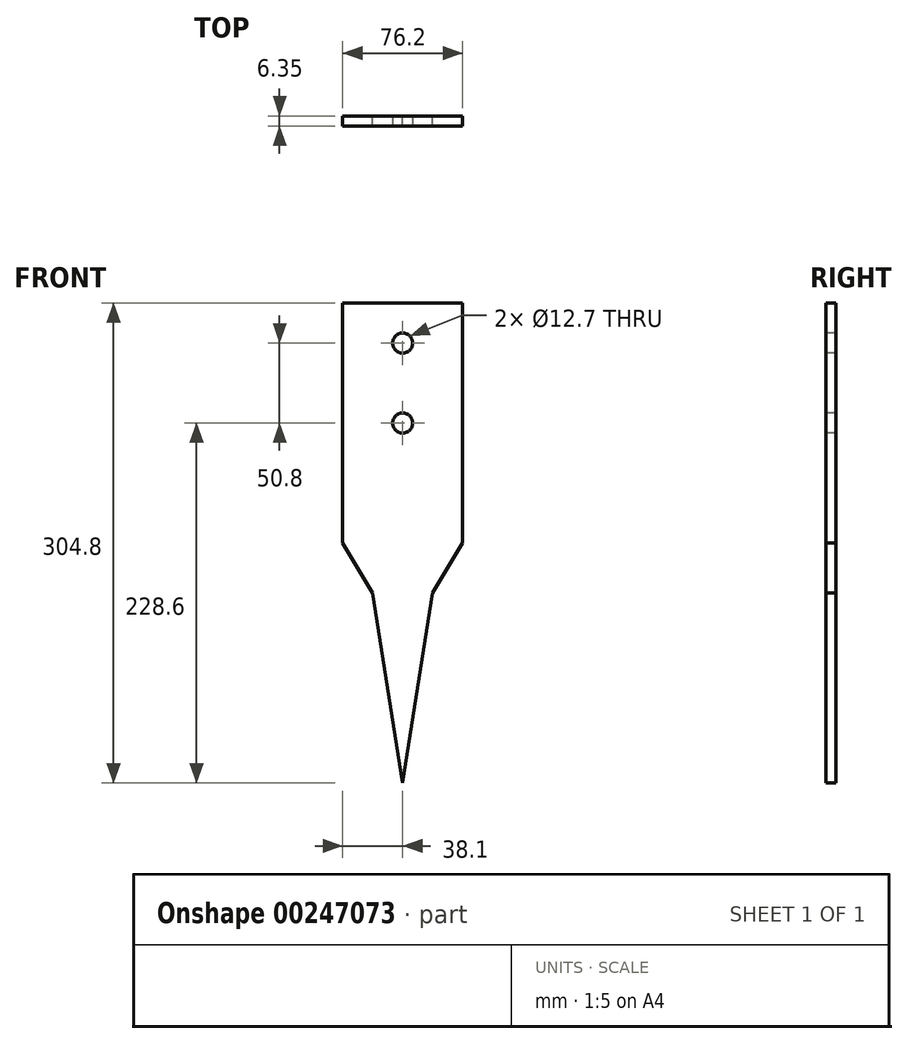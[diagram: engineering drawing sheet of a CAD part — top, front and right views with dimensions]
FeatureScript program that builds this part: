
annotation { "Feature Type Name" : "Feature", "Feature Type Description" : "" }
export const myFeature = defineFeature(function(context is Context, id is Id, definition is map)
    precondition{}
    {
        {
            var Q0;
            Q0=qCreatedBy(makeId("Front.planeOp"),FACE);
            var sketch = newSketch(context, id + "F0", { "sketchPlane" : qUnion([Q0])});
            skLineSegment(sketch, "E0.bottom", {"start": v(38.1, 76.2) * mm, "end": v(-38.1, 76.2) * mm});
            skLineSegment(sketch, "E0.top", {"start": v(38.1, -76.2) * mm, "end": v(-38.1, -76.2) * mm});
            skLineSegment(sketch, "E0.left", {"start": v(38.1, 76.2) * mm, "end": v(38.1, -76.2) * mm});
            skLineSegment(sketch, "E0.right", {"start": v(-38.1, 76.2) * mm, "end": v(-38.1, -76.2) * mm});
            skPoint(sketch, "E0.middle", {"position": v(0, 0) * mm});
            skLineSegment(sketch, "E1", {"start": v(38.1, -76.2) * mm, "end": v(19.05, -107.95) * mm});
            skLineSegment(sketch, "E2", {"start": v(19.05, -107.95) * mm, "end": v(0, -228.6) * mm});
            skLineSegment(sketch, "E3", {"start": v(0, -228.6) * mm, "end": v(-19.05, -107.95) * mm});
            skLineSegment(sketch, "E4", {"start": v(-19.05, -107.95) * mm, "end": v(-38.1, -76.2) * mm});
            skSolve(sketch);
        }
        {
            var Q0;
            Q0=makeQuery(id+"F0.imprint","IMPRINT",FACE,{"disambiguationData":[TD([[makeQuery(id+"F0.imprint","IMPRINT",EDGE,{"derivedFrom":sQuery(id+"F0.wireOp",EDGE,"E0.bottom")}),1.0]])]});
            var Q1;
            Q1=makeQuery(id+"F0.imprint","IMPRINT",FACE,{"disambiguationData":[TD([[makeQuery(id+"F0.imprint","IMPRINT",EDGE,{"derivedFrom":sQuery(id+"F0.wireOp",EDGE,"E0.top")}),1.0]])]});
            extrude(context, id + "F1", {"entities" : qUnion([Q0, Q1]), "depth" : 6.35 * mm});
        }
        {
            var Q0;
            Q0=makeQuery(id+"F1.opExtrude","CAP_FACE",FACE,{"disambiguationData":[OSD([sQuery(id+"F0.wireOp",EDGE,"E0.bottom"),sQuery(id+"F0.wireOp",EDGE,"E0.left"),sQuery(id+"F0.wireOp",EDGE,"E0.right"),sQuery(id+"F0.wireOp",EDGE,"E1"),sQuery(id+"F0.wireOp",EDGE,"E2"),sQuery(id+"F0.wireOp",EDGE,"E3"),sQuery(id+"F0.wireOp",EDGE,"E4")])],"isStart":false});
            var sketch = newSketch(context, id + "F2", { "sketchPlane" : qUnion([Q0])});
            skCircle(sketch, "E5", {"center": v(0, 50.8) * mm, "radius": 6.35 * mm});
            skCircle(sketch, "E6", {"center": v(0, 0) * mm, "radius": 6.35 * mm});
            skSolve(sketch);
        }
        {
            var Q0;
            Q0 = qSketchRegion(id + "F2", true);
            extrude(context, id + "F3", {"entities" : qUnion([Q0]), "operationType" : NewBodyOperationType.REMOVE, "oppositeDirection" : true, "depth" : 25.4 * mm});
        }
    });
